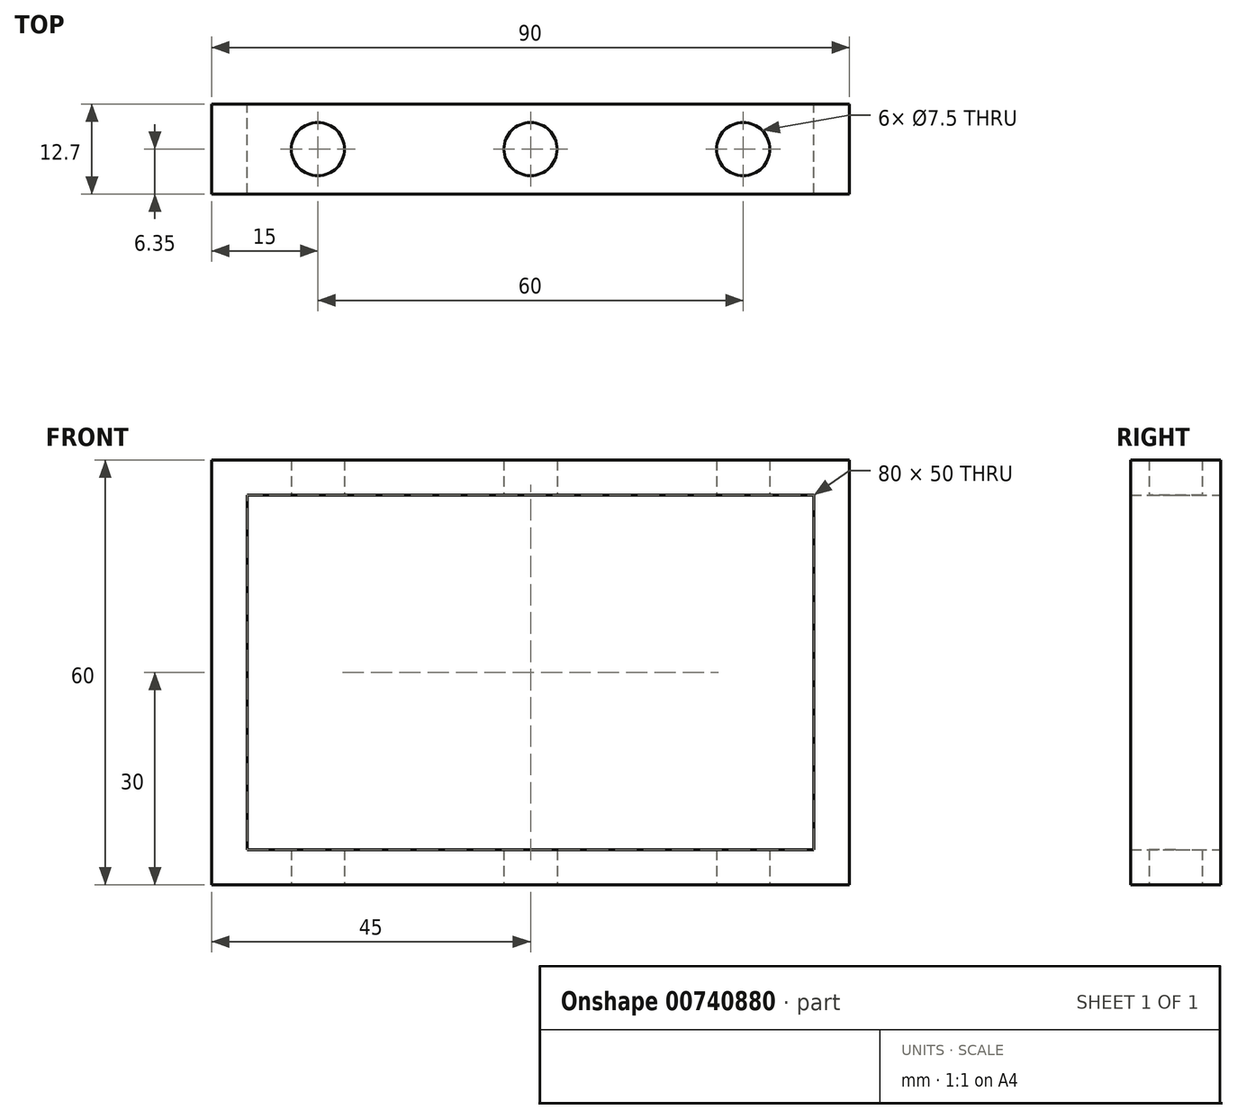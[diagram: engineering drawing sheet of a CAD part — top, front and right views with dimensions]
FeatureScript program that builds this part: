
annotation { "Feature Type Name" : "Feature", "Feature Type Description" : "" }
export const myFeature = defineFeature(function(context is Context, id is Id, definition is map)
    precondition{}
    {
        {
            var Q0;
            Q0=qCreatedBy(makeId("Front.planeOp"),FACE);
            var sketch = newSketch(context, id + "F0", { "sketchPlane" : qUnion([Q0])});
            skLineSegment(sketch, "E0.bottom", {"start": v(-45, 30) * mm, "end": v(45, 30) * mm});
            skLineSegment(sketch, "E0.top", {"start": v(-45, -30) * mm, "end": v(45, -30) * mm});
            skLineSegment(sketch, "E0.left", {"start": v(-45, 30) * mm, "end": v(-45, -30) * mm});
            skLineSegment(sketch, "E0.right", {"start": v(45, 30) * mm, "end": v(45, -30) * mm});
            skLineSegment(sketch, "E1.bottom", {"start": v(-40, 25) * mm, "end": v(40, 25) * mm});
            skLineSegment(sketch, "E1.top", {"start": v(-40, -25) * mm, "end": v(40, -25) * mm});
            skLineSegment(sketch, "E1.left", {"start": v(-40, 25) * mm, "end": v(-40, -25) * mm});
            skLineSegment(sketch, "E1.right", {"start": v(40, 25) * mm, "end": v(40, -25) * mm});
            skSolve(sketch);
        }
        {
            var Q0;
            Q0=makeQuery(id+"F0.imprint","IMPRINT",FACE,{"disambiguationData":[TD([[makeQuery(id+"F0.imprint","IMPRINT",EDGE,{"derivedFrom":sQuery(id+"F0.wireOp",EDGE,"E0.bottom")}),-1.0]])]});
            var Q1;
            Q1 = qSketchRegion(id + "F2", true);
            extrude(context, id + "F1", {"entities" : qUnion([Q0, Q1]), "depth" : 12.7 * mm, "offsetDistance" : 25.4 * mm});
        }
        {
            var Q0;
            Q0=makeQuery(id+"F1.opExtrude","SWEPT_FACE",FACE,{"disambiguationData":[OSD([sQuery(id+"F0.wireOp",EDGE,"E0.top")])]});
            var sketch = newSketch(context, id + "F2", { "sketchPlane" : qUnion([Q0])});
            skCircle(sketch, "E2", {"center": v(0, 6.35) * mm, "radius": 3.75 * mm});
            skCircle(sketch, "E3", {"center": v(-30, 6.35) * mm, "radius": 3.75 * mm});
            skCircle(sketch, "E4", {"center": v(30, 6.35) * mm, "radius": 3.75 * mm});
            skSolve(sketch);
        }
        {
            var Q0;
            Q0=makeQuery(id+"F2.imprint","IMPRINT",FACE,{"disambiguationData":[TD([[makeQuery(id+"F2.imprint","IMPRINT",EDGE,{"derivedFrom":sQuery(id+"F2.wireOp",EDGE,"E3")}),1.0]])]});
            var Q1;
            Q1=makeQuery(id+"F2.imprint","IMPRINT",FACE,{"disambiguationData":[TD([[makeQuery(id+"F2.imprint","IMPRINT",EDGE,{"derivedFrom":sQuery(id+"F2.wireOp",EDGE,"E2")}),1.0]])]});
            var Q2;
            Q2=makeQuery(id+"F2.imprint","IMPRINT",FACE,{"disambiguationData":[TD([[makeQuery(id+"F2.imprint","IMPRINT",EDGE,{"derivedFrom":sQuery(id+"F2.wireOp",EDGE,"E4")}),1.0]])]});
            extrude(context, id + "F3", {"entities" : qUnion([Q0, Q1, Q2]), "operationType" : NewBodyOperationType.REMOVE, "oppositeDirection" : true, "depth" : 76.2 * mm, "offsetDistance" : 25.4 * mm});
        }
    });
